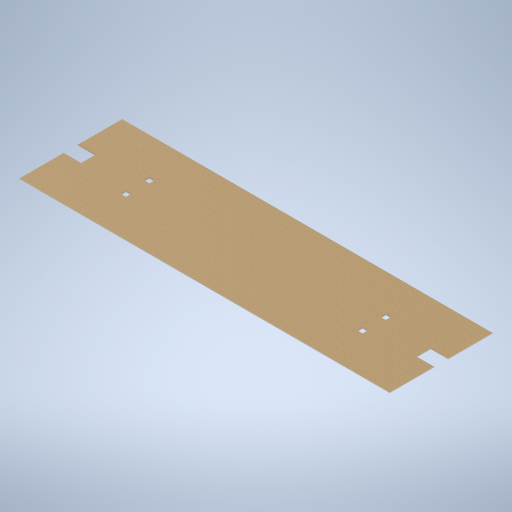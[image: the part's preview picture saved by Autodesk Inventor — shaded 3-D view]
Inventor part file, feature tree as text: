
AUTODESK INVENTOR PART (.ipt)
format: ipt  version: 2024.2 (Build 282272000, 272)  size: 317,952 bytes
history: native  units: mm
features: extrude x1, sketch x1
ambient origin geometry x8: Origin, YZ Plane, XZ Plane, XY Plane, X Axis, Y Axis, Z Axis, Center Point
bodies: Solid1 (feature_tree)
feature tree (2):
  extrude  "Extrusion1"  Depth=1500.0mm
  sketch  "Sketch1"  dims[d0=1500.0mm d1=1500.0mm d2=40.0mm d3=0.0mm]
